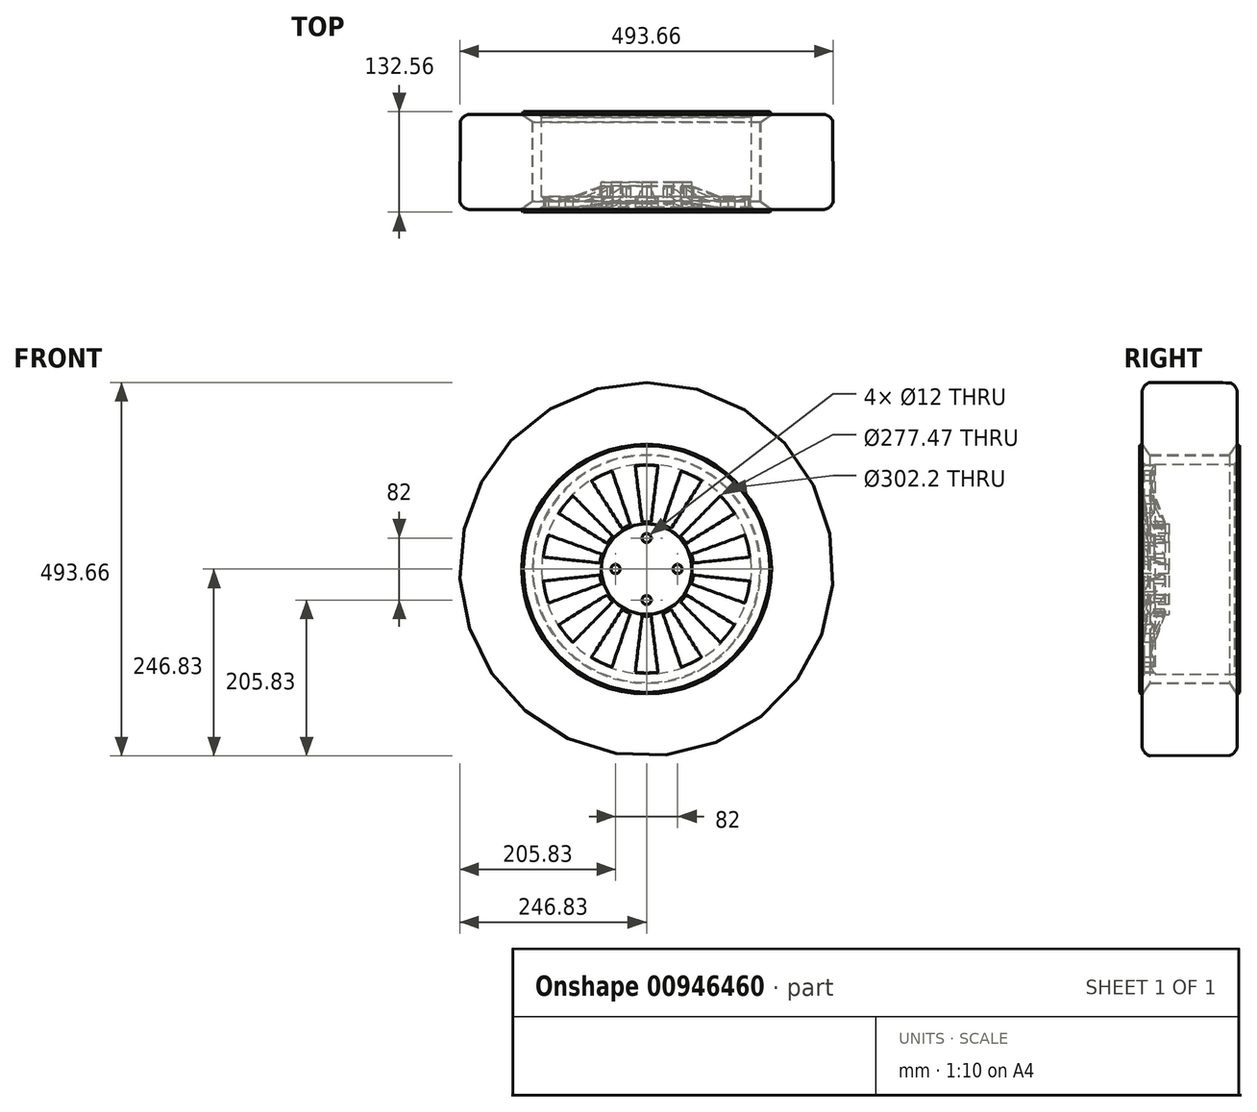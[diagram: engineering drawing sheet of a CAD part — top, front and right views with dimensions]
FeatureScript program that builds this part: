
annotation { "Feature Type Name" : "Feature", "Feature Type Description" : "" }
export const myFeature = defineFeature(function(context is Context, id is Id, definition is map)
    precondition{}
    {
        {
            var Q0;
            Q0=qCreatedBy(makeId("Right.planeOp"),FACE);
            var sketch = newSketch(context, id + "F0", { "sketchPlane" : qUnion([Q0])});
            skLineSegment(sketch, "E0", {"start": v(0, 0) * mm, "end": v(-305.68, 0) * mm, "construction": true});
            skLineSegment(sketch, "E1", {"start": v(-125, 0) * mm, "end": v(-125, 60) * mm});
            skLineSegment(sketch, "E2", {"start": v(-125, 60) * mm, "end": v(-118, 60) * mm});
            skLineSegment(sketch, "E3", {"start": v(0, 0) * mm, "end": v(0, 165.1) * mm, "construction": true});
            skLineSegment(sketch, "E4", {"start": v(0, 165.1) * mm, "end": v(-10.5, 150.1) * mm});
            skLineSegment(sketch, "E5", {"start": v(-10.5, 150.1) * mm, "end": v(-115.5, 150.1) * mm});
            skLineSegment(sketch, "E6", {"start": v(-115.5, 150.1) * mm, "end": v(-126, 165.1) * mm});
            skLineSegment(sketch, "E7", {"start": v(-126, 165.1) * mm, "end": v(-129.28, 162.8) * mm});
            skLineSegment(sketch, "E8", {"start": v(0, 165.1) * mm, "end": v(3.28, 162.8) * mm});
            skLineSegment(sketch, "E9", {"start": v(-129.28, 162.8) * mm, "end": v(-129.28, 147.88) * mm});
            skLineSegment(sketch, "E10", {"start": v(-127.82, 144.34) * mm, "end": v(-123.4, 139.92) * mm});
            skLineSegment(sketch, "E11", {"start": v(-63, 150.1) * mm, "end": v(-63, 101.93) * mm, "construction": true});
            skLineSegment(sketch, "E12.MirrorCS", {"start": v(1.81, 144.34) * mm, "end": v(-3.8, 138.73) * mm});
            skLineSegment(sketch, "E13.MirrorCS", {"start": v(3.28, 162.8) * mm, "end": v(3.28, 147.88) * mm});
            skFitSpline(sketch, "E14", {"points": [v(-118, 60) * mm, v(-127.97, 115.77) * mm, v(-122.21, 138.73) * mm], "startDerivative": vector(-12.1, 140.22) * mm, "endDerivative": vector(53.59, 74.72) * mm});
            skArc(sketch, "E15.filletArc", {"start": v(-123.15, 137.38) * mm, "mid": v(-122.82, 138.7) * mm, "end": v(-123.4, 139.92) * mm});
            skPoint(sketch, "E16.visualSharp", {"position": v(-129.28, 145.8) * mm});
            skArc(sketch, "E16.filletArc", {"start": v(-129.28, 147.88) * mm, "mid": v(-128.9, 145.96) * mm, "end": v(-127.82, 144.34) * mm});
            skPoint(sketch, "E17.visualSharp", {"position": v(3.28, 145.8) * mm});
            skArc(sketch, "E17.filletArc", {"start": v(1.81, 144.34) * mm, "mid": v(2.9, 145.96) * mm, "end": v(3.28, 147.88) * mm});
            skLineSegment(sketch, "E18", {"start": v(-3.8, 138.73) * mm, "end": v(-108.8, 138.73) * mm});
            skLineSegment(sketch, "E19", {"start": v(-95, 60) * mm, "end": v(-90, 60) * mm});
            skLineSegment(sketch, "E20", {"start": v(-90, 60) * mm, "end": v(-90, 0) * mm});
            skLineSegment(sketch, "E21", {"start": v(-90, 0) * mm, "end": v(-125, 0) * mm});
            skFitSpline(sketch, "E22", {"points": [v(-95, 60) * mm, v(-114.6, 118.9) * mm, v(-108.8, 138.73) * mm], "startDerivative": vector(-64.42, 180.65) * mm, "endDerivative": vector(44.77, 42.27) * mm});
            skLineSegment(sketch, "E23", {"start": v(-115.5, 151.1) * mm, "end": v(-10.5, 151.1) * mm});
            skLineSegment(sketch, "E24", {"start": v(-10.5, 151.1) * mm, "end": v(-3.62, 160.93) * mm});
            skLineSegment(sketch, "E25", {"start": v(0, 172.4) * mm, "end": v(0, 232.44) * mm});
            skLineSegment(sketch, "E26", {"start": v(-7.5, 245.43) * mm, "end": v(-7.61, 245.5) * mm});
            skLineSegment(sketch, "E27", {"start": v(-10.08, 246.17) * mm, "end": v(-114.7, 246.83) * mm});
            skLineSegment(sketch, "E28", {"start": v(-118.5, 245.43) * mm, "end": v(-117.24, 246.16) * mm});
            skLineSegment(sketch, "E29", {"start": v(-126, 232.44) * mm, "end": v(-126, 172.4) * mm});
            skLineSegment(sketch, "E30", {"start": v(-122.39, 160.93) * mm, "end": v(-115.5, 151.1) * mm});
            skLineSegment(sketch, "E31", {"start": v(-115.5, 150.1) * mm, "end": v(-115.5, 151.1) * mm});
            skLineSegment(sketch, "E32", {"start": v(-10.5, 150.1) * mm, "end": v(-10.5, 151.1) * mm});
            skPoint(sketch, "E33.visualSharp", {"position": v(-116.06, 246.84) * mm});
            skArc(sketch, "E33.filletArc", {"start": v(-114.7, 246.83) * mm, "mid": v(-116.02, 246.67) * mm, "end": v(-117.24, 246.16) * mm});
            skPoint(sketch, "E34.visualSharp", {"position": v(-8.76, 246.16) * mm});
            skArc(sketch, "E34.filletArc", {"start": v(-7.61, 245.5) * mm, "mid": v(-8.8, 246) * mm, "end": v(-10.08, 246.17) * mm});
            skPoint(sketch, "E35.visualSharp", {"position": v(0, 241.1) * mm});
            skArc(sketch, "E35.filletArc", {"start": v(0, 232.44) * mm, "mid": v(-2, 239.94) * mm, "end": v(-7.5, 245.43) * mm});
            skPoint(sketch, "E36.visualSharp", {"position": v(-126, 241.1) * mm});
            skArc(sketch, "E36.filletArc", {"start": v(-118.5, 245.43) * mm, "mid": v(-124, 239.94) * mm, "end": v(-126, 232.44) * mm});
            skPoint(sketch, "E37.visualSharp", {"position": v(-126, 166.1) * mm});
            skArc(sketch, "E37.filletArc", {"start": v(-126, 172.4) * mm, "mid": v(-125.08, 166.4) * mm, "end": v(-122.39, 160.93) * mm});
            skPoint(sketch, "E38.visualSharp", {"position": v(0, 166.1) * mm});
            skArc(sketch, "E38.filletArc", {"start": v(-3.62, 160.93) * mm, "mid": v(-0.93, 166.4) * mm, "end": v(0, 172.4) * mm});
            skSolve(sketch);
        }
        {
            var Q0;
            Q0=makeQuery(id+"F0.imprint","IMPRINT",FACE,{"disambiguationData":[TD([[makeQuery(id+"F0.imprint","IMPRINT",EDGE,{"derivedFrom":sQuery(id+"F0.wireOp",EDGE,"E23")}),1.0]])]});
            var Q1;
            Q1=makeQuery(id+"F0.imprint","IMPRINT",FACE,{"disambiguationData":[TD([[makeQuery(id+"F0.imprint","IMPRINT",EDGE,{"derivedFrom":sQuery(id+"F0.wireOp",EDGE,"E1")}),-1.0]])]});
            var Q2;
            Q2=sQuery(id+"F0.wireOp",EDGE,"E0");
            revolve(context, id + "F1", {"surfaceOperationType" : NewSurfaceOperationType.NEW, "entities" : qUnion([Q0, Q1]), "axis" : qUnion([Q2]), "revolveType" : RevolveType.FULL});
        }
        {
            var Q0;
            Q0=qCreatedBy(makeId("Front.planeOp"),FACE);
            cPlane(context, id + "F2", {"entities" : qUnion([Q0]), "cplaneType" : CPlaneType.OFFSET, "offset" : 140 * mm, "width" : 150 * mm, "height" : 150 * mm});
        }
        {
            var Q0;
            Q0=qCreatedBy(id+"F2.planeOp",FACE);
            var sketch = newSketch(context, id + "F3", { "sketchPlane" : qUnion([Q0])});
            skCircle(sketch, "E39", {"center": v(0, 0) * mm, "radius": 62.5 * mm, "construction": true});
            skCircle(sketch, "E40", {"center": v(0, 0) * mm, "radius": 137.5 * mm, "construction": true});
            skLineSegment(sketch, "E41", {"start": v(0, 62.5) * mm, "end": v(0, 137.5) * mm, "construction": true});
            skLineSegment(sketch, "E42", {"start": v(-6, 62.21) * mm, "end": v(-15, 136.68) * mm});
            skLineSegment(sketch, "E43", {"start": v(-15, 136.68) * mm, "end": v(0, 137.5) * mm});
            skLineSegment(sketch, "E44", {"start": v(-6, 62.21) * mm, "end": v(0, 62.5) * mm});
            skLineSegment(sketch, "E45.MirrorCS", {"start": v(6, 62.21) * mm, "end": v(15, 136.68) * mm});
            skLineSegment(sketch, "E46.MirrorCS", {"start": v(15, 136.68) * mm, "end": v(0, 137.5) * mm});
            skLineSegment(sketch, "E47.MirrorCS", {"start": v(6, 62.21) * mm, "end": v(0, 62.5) * mm});
            skLineSegment(sketch, "E48.1.0", {"start": v(-21.6, 58.65) * mm, "end": v(-27.12, 56.31) * mm});
            skLineSegment(sketch, "E48.1.1", {"start": v(-21.6, 58.65) * mm, "end": v(-45.79, 129.65) * mm});
            skLineSegment(sketch, "E48.1.2", {"start": v(-32.4, 53.45) * mm, "end": v(-27.12, 56.31) * mm});
            skLineSegment(sketch, "E48.1.3", {"start": v(-32.4, 53.45) * mm, "end": v(-72.82, 116.64) * mm});
            skLineSegment(sketch, "E48.1.4", {"start": v(-45.79, 129.65) * mm, "end": v(-59.66, 123.88) * mm});
            skLineSegment(sketch, "E48.1.5", {"start": v(-72.82, 116.64) * mm, "end": v(-59.66, 123.88) * mm});
            skLineSegment(sketch, "E48.2.0", {"start": v(-44.9, 43.47) * mm, "end": v(-48.86, 38.97) * mm});
            skLineSegment(sketch, "E48.2.1", {"start": v(-44.9, 43.47) * mm, "end": v(-97.5, 96.95) * mm});
            skLineSegment(sketch, "E48.2.2", {"start": v(-52.38, 34.1) * mm, "end": v(-48.86, 38.97) * mm});
            skLineSegment(sketch, "E48.2.3", {"start": v(-52.38, 34.1) * mm, "end": v(-116.21, 73.5) * mm});
            skLineSegment(sketch, "E48.2.4", {"start": v(-97.5, 96.95) * mm, "end": v(-107.5, 85.73) * mm});
            skLineSegment(sketch, "E48.2.5", {"start": v(-116.21, 73.5) * mm, "end": v(-107.5, 85.73) * mm});
            skLineSegment(sketch, "E48.3.0", {"start": v(-59.32, 19.69) * mm, "end": v(-60.93, 13.9) * mm});
            skLineSegment(sketch, "E48.3.1", {"start": v(-59.32, 19.69) * mm, "end": v(-129.91, 45.04) * mm});
            skLineSegment(sketch, "E48.3.2", {"start": v(-61.99, 8) * mm, "end": v(-60.93, 13.9) * mm});
            skLineSegment(sketch, "E48.3.3", {"start": v(-61.99, 8) * mm, "end": v(-136.6, 15.8) * mm});
            skLineSegment(sketch, "E48.3.4", {"start": v(-129.91, 45.04) * mm, "end": v(-134.05, 30.6) * mm});
            skLineSegment(sketch, "E48.3.5", {"start": v(-136.6, 15.8) * mm, "end": v(-134.05, 30.6) * mm});
            skLineSegment(sketch, "E48.4.0", {"start": v(-61.99, -8) * mm, "end": v(-60.93, -13.9) * mm});
            skLineSegment(sketch, "E48.4.1", {"start": v(-61.99, -8) * mm, "end": v(-136.6, -15.8) * mm});
            skLineSegment(sketch, "E48.4.2", {"start": v(-59.32, -19.69) * mm, "end": v(-60.93, -13.9) * mm});
            skLineSegment(sketch, "E48.4.3", {"start": v(-59.32, -19.69) * mm, "end": v(-129.91, -45.04) * mm});
            skLineSegment(sketch, "E48.4.4", {"start": v(-136.6, -15.8) * mm, "end": v(-134.05, -30.6) * mm});
            skLineSegment(sketch, "E48.4.5", {"start": v(-129.91, -45.04) * mm, "end": v(-134.05, -30.6) * mm});
            skLineSegment(sketch, "E48.5.0", {"start": v(-52.38, -34.1) * mm, "end": v(-48.86, -38.97) * mm});
            skLineSegment(sketch, "E48.5.1", {"start": v(-52.38, -34.1) * mm, "end": v(-116.21, -73.5) * mm});
            skLineSegment(sketch, "E48.5.2", {"start": v(-44.9, -43.47) * mm, "end": v(-48.86, -38.97) * mm});
            skLineSegment(sketch, "E48.5.3", {"start": v(-44.9, -43.47) * mm, "end": v(-97.5, -96.95) * mm});
            skLineSegment(sketch, "E48.5.4", {"start": v(-116.21, -73.5) * mm, "end": v(-107.5, -85.73) * mm});
            skLineSegment(sketch, "E48.5.5", {"start": v(-97.5, -96.95) * mm, "end": v(-107.5, -85.73) * mm});
            skLineSegment(sketch, "E48.6.0", {"start": v(-32.4, -53.45) * mm, "end": v(-27.12, -56.31) * mm});
            skLineSegment(sketch, "E48.6.1", {"start": v(-32.4, -53.45) * mm, "end": v(-72.82, -116.64) * mm});
            skLineSegment(sketch, "E48.6.2", {"start": v(-21.6, -58.65) * mm, "end": v(-27.12, -56.31) * mm});
            skLineSegment(sketch, "E48.6.3", {"start": v(-21.6, -58.65) * mm, "end": v(-45.79, -129.65) * mm});
            skLineSegment(sketch, "E48.6.4", {"start": v(-72.82, -116.64) * mm, "end": v(-59.66, -123.88) * mm});
            skLineSegment(sketch, "E48.6.5", {"start": v(-45.79, -129.65) * mm, "end": v(-59.66, -123.88) * mm});
            skLineSegment(sketch, "E48.7.0", {"start": v(-6, -62.21) * mm, "end": v(0, -62.5) * mm});
            skLineSegment(sketch, "E48.7.1", {"start": v(-6, -62.21) * mm, "end": v(-15, -136.68) * mm});
            skLineSegment(sketch, "E48.7.2", {"start": v(6, -62.21) * mm, "end": v(0, -62.5) * mm});
            skLineSegment(sketch, "E48.7.3", {"start": v(6, -62.21) * mm, "end": v(15, -136.68) * mm});
            skLineSegment(sketch, "E48.7.4", {"start": v(-15, -136.68) * mm, "end": v(0, -137.5) * mm});
            skLineSegment(sketch, "E48.7.5", {"start": v(15, -136.68) * mm, "end": v(0, -137.5) * mm});
            skLineSegment(sketch, "E48.8.0", {"start": v(21.6, -58.65) * mm, "end": v(27.12, -56.31) * mm});
            skLineSegment(sketch, "E48.8.1", {"start": v(21.6, -58.65) * mm, "end": v(45.79, -129.65) * mm});
            skLineSegment(sketch, "E48.8.2", {"start": v(32.4, -53.45) * mm, "end": v(27.12, -56.31) * mm});
            skLineSegment(sketch, "E48.8.3", {"start": v(32.4, -53.45) * mm, "end": v(72.82, -116.64) * mm});
            skLineSegment(sketch, "E48.8.4", {"start": v(45.79, -129.65) * mm, "end": v(59.66, -123.88) * mm});
            skLineSegment(sketch, "E48.8.5", {"start": v(72.82, -116.64) * mm, "end": v(59.66, -123.88) * mm});
            skLineSegment(sketch, "E48.9.0", {"start": v(44.9, -43.47) * mm, "end": v(48.86, -38.97) * mm});
            skLineSegment(sketch, "E48.9.1", {"start": v(44.9, -43.47) * mm, "end": v(97.5, -96.95) * mm});
            skLineSegment(sketch, "E48.9.2", {"start": v(52.38, -34.1) * mm, "end": v(48.86, -38.97) * mm});
            skLineSegment(sketch, "E48.9.3", {"start": v(52.38, -34.1) * mm, "end": v(116.21, -73.5) * mm});
            skLineSegment(sketch, "E48.9.4", {"start": v(97.5, -96.95) * mm, "end": v(107.5, -85.73) * mm});
            skLineSegment(sketch, "E48.9.5", {"start": v(116.21, -73.5) * mm, "end": v(107.5, -85.73) * mm});
            skLineSegment(sketch, "E48.10.0", {"start": v(59.32, -19.69) * mm, "end": v(60.93, -13.9) * mm});
            skLineSegment(sketch, "E48.10.1", {"start": v(59.32, -19.69) * mm, "end": v(129.91, -45.04) * mm});
            skLineSegment(sketch, "E48.10.2", {"start": v(61.99, -8) * mm, "end": v(60.93, -13.9) * mm});
            skLineSegment(sketch, "E48.10.3", {"start": v(61.99, -8) * mm, "end": v(136.6, -15.8) * mm});
            skLineSegment(sketch, "E48.10.4", {"start": v(129.91, -45.04) * mm, "end": v(134.05, -30.6) * mm});
            skLineSegment(sketch, "E48.10.5", {"start": v(136.6, -15.8) * mm, "end": v(134.05, -30.6) * mm});
            skLineSegment(sketch, "E48.11.0", {"start": v(61.99, 8) * mm, "end": v(60.93, 13.9) * mm});
            skLineSegment(sketch, "E48.11.1", {"start": v(61.99, 8) * mm, "end": v(136.6, 15.8) * mm});
            skLineSegment(sketch, "E48.11.2", {"start": v(59.32, 19.69) * mm, "end": v(60.93, 13.9) * mm});
            skLineSegment(sketch, "E48.11.3", {"start": v(59.32, 19.69) * mm, "end": v(129.91, 45.04) * mm});
            skLineSegment(sketch, "E48.11.4", {"start": v(136.6, 15.8) * mm, "end": v(134.05, 30.6) * mm});
            skLineSegment(sketch, "E48.11.5", {"start": v(129.91, 45.04) * mm, "end": v(134.05, 30.6) * mm});
            skLineSegment(sketch, "E48.12.0", {"start": v(52.38, 34.1) * mm, "end": v(48.86, 38.97) * mm});
            skLineSegment(sketch, "E48.12.1", {"start": v(52.38, 34.1) * mm, "end": v(116.21, 73.5) * mm});
            skLineSegment(sketch, "E48.12.2", {"start": v(44.9, 43.47) * mm, "end": v(48.86, 38.97) * mm});
            skLineSegment(sketch, "E48.12.3", {"start": v(44.9, 43.47) * mm, "end": v(97.5, 96.95) * mm});
            skLineSegment(sketch, "E48.12.4", {"start": v(116.21, 73.5) * mm, "end": v(107.5, 85.73) * mm});
            skLineSegment(sketch, "E48.12.5", {"start": v(97.5, 96.95) * mm, "end": v(107.5, 85.73) * mm});
            skLineSegment(sketch, "E48.13.0", {"start": v(32.4, 53.45) * mm, "end": v(27.12, 56.31) * mm});
            skLineSegment(sketch, "E48.13.1", {"start": v(32.4, 53.45) * mm, "end": v(72.82, 116.64) * mm});
            skLineSegment(sketch, "E48.13.2", {"start": v(21.6, 58.65) * mm, "end": v(27.12, 56.31) * mm});
            skLineSegment(sketch, "E48.13.3", {"start": v(21.6, 58.65) * mm, "end": v(45.79, 129.65) * mm});
            skLineSegment(sketch, "E48.13.4", {"start": v(72.82, 116.64) * mm, "end": v(59.66, 123.88) * mm});
            skLineSegment(sketch, "E48.13.5", {"start": v(45.79, 129.65) * mm, "end": v(59.66, 123.88) * mm});
            skSolve(sketch);
        }
        {
            var Q0;
            Q0=makeQuery(id+"F3.imprint","IMPRINT",FACE,{"disambiguationData":[TD([[makeQuery(id+"F3.imprint","IMPRINT",EDGE,{"derivedFrom":sQuery(id+"F3.wireOp",EDGE,"E48.1.0")}),-1.0]])]});
            var Q1;
            Q1=makeQuery(id+"F3.imprint","IMPRINT",FACE,{"disambiguationData":[TD([[makeQuery(id+"F3.imprint","IMPRINT",EDGE,{"derivedFrom":sQuery(id+"F3.wireOp",EDGE,"E42")}),-1.0]])]});
            var Q2;
            Q2=makeQuery(id+"F3.imprint","IMPRINT",FACE,{"disambiguationData":[TD([[makeQuery(id+"F3.imprint","IMPRINT",EDGE,{"derivedFrom":sQuery(id+"F3.wireOp",EDGE,"E48.13.0")}),-1.0]])]});
            var Q3;
            Q3=makeQuery(id+"F3.imprint","IMPRINT",FACE,{"disambiguationData":[TD([[makeQuery(id+"F3.imprint","IMPRINT",EDGE,{"derivedFrom":sQuery(id+"F3.wireOp",EDGE,"E48.12.0")}),-1.0]])]});
            var Q4;
            Q4=makeQuery(id+"F3.imprint","IMPRINT",FACE,{"disambiguationData":[TD([[makeQuery(id+"F3.imprint","IMPRINT",EDGE,{"derivedFrom":sQuery(id+"F3.wireOp",EDGE,"E48.11.0")}),-1.0]])]});
            var Q5;
            Q5=makeQuery(id+"F3.imprint","IMPRINT",FACE,{"disambiguationData":[TD([[makeQuery(id+"F3.imprint","IMPRINT",EDGE,{"derivedFrom":sQuery(id+"F3.wireOp",EDGE,"E48.10.0")}),-1.0]])]});
            var Q6;
            Q6=makeQuery(id+"F3.imprint","IMPRINT",FACE,{"disambiguationData":[TD([[makeQuery(id+"F3.imprint","IMPRINT",EDGE,{"derivedFrom":sQuery(id+"F3.wireOp",EDGE,"E48.9.0")}),-1.0]])]});
            var Q7;
            Q7=makeQuery(id+"F3.imprint","IMPRINT",FACE,{"disambiguationData":[TD([[makeQuery(id+"F3.imprint","IMPRINT",EDGE,{"derivedFrom":sQuery(id+"F3.wireOp",EDGE,"E48.8.0")}),-1.0]])]});
            var Q8;
            Q8=makeQuery(id+"F3.imprint","IMPRINT",FACE,{"disambiguationData":[TD([[makeQuery(id+"F3.imprint","IMPRINT",EDGE,{"derivedFrom":sQuery(id+"F3.wireOp",EDGE,"E48.7.0")}),-1.0]])]});
            var Q9;
            Q9=makeQuery(id+"F3.imprint","IMPRINT",FACE,{"disambiguationData":[TD([[makeQuery(id+"F3.imprint","IMPRINT",EDGE,{"derivedFrom":sQuery(id+"F3.wireOp",EDGE,"E48.6.0")}),-1.0]])]});
            var Q10;
            Q10=makeQuery(id+"F3.imprint","IMPRINT",FACE,{"disambiguationData":[TD([[makeQuery(id+"F3.imprint","IMPRINT",EDGE,{"derivedFrom":sQuery(id+"F3.wireOp",EDGE,"E48.5.0")}),-1.0]])]});
            var Q11;
            Q11=makeQuery(id+"F3.imprint","IMPRINT",FACE,{"disambiguationData":[TD([[makeQuery(id+"F3.imprint","IMPRINT",EDGE,{"derivedFrom":sQuery(id+"F3.wireOp",EDGE,"E48.4.0")}),-1.0]])]});
            var Q12;
            Q12=makeQuery(id+"F3.imprint","IMPRINT",FACE,{"disambiguationData":[TD([[makeQuery(id+"F3.imprint","IMPRINT",EDGE,{"derivedFrom":sQuery(id+"F3.wireOp",EDGE,"E48.3.0")}),-1.0]])]});
            var Q13;
            Q13=makeQuery(id+"F3.imprint","IMPRINT",FACE,{"disambiguationData":[TD([[makeQuery(id+"F3.imprint","IMPRINT",EDGE,{"derivedFrom":sQuery(id+"F3.wireOp",EDGE,"E48.2.0")}),-1.0]])]});
            extrude(context, id + "F4", {"entities" : qUnion([Q0, Q1, Q2, Q3, Q4, Q5, Q6, Q7, Q8, Q9, Q10, Q11, Q12, Q13]), "operationType" : NewBodyOperationType.REMOVE, "oppositeDirection" : true, "depth" : 150 * mm, "offsetDistance" : 25 * mm});
        }
        {
            var Q0;
            Q0=makeQuery(id+"F1.opRevolve","SWEPT_FACE",FACE,{"disambiguationData":[OSD([sQuery(id+"F0.wireOp",EDGE,"E1")])]});
            var sketch = newSketch(context, id + "F5", { "sketchPlane" : qUnion([Q0])});
            skLineSegment(sketch, "E49", {"start": v(0, 0) * mm, "end": v(0, 41) * mm, "construction": true});
            skCircle(sketch, "E50", {"center": v(0, 41) * mm, "radius": 6 * mm});
            skCircle(sketch, "E51.1.0", {"center": v(-41, 0) * mm, "radius": 6 * mm});
            skCircle(sketch, "E51.2.0", {"center": v(0, -41) * mm, "radius": 6 * mm});
            skCircle(sketch, "E51.3.0", {"center": v(41, 0) * mm, "radius": 6 * mm});
            skPoint(sketch, "E51.center", {"position": v(0, 0) * mm});
            skSolve(sketch);
        }
        {
            var Q0;
            Q0=makeQuery(id+"F5.imprint","IMPRINT",FACE,{"disambiguationData":[TD([[makeQuery(id+"F5.imprint","IMPRINT",EDGE,{"derivedFrom":sQuery(id+"F5.wireOp",EDGE,"E50")}),1.0]])]});
            var Q1;
            Q1=makeQuery(id+"F5.imprint","IMPRINT",FACE,{"disambiguationData":[TD([[makeQuery(id+"F5.imprint","IMPRINT",EDGE,{"derivedFrom":sQuery(id+"F5.wireOp",EDGE,"E51.3.0")}),1.0]])]});
            var Q2;
            Q2=makeQuery(id+"F5.imprint","IMPRINT",FACE,{"disambiguationData":[TD([[makeQuery(id+"F5.imprint","IMPRINT",EDGE,{"derivedFrom":sQuery(id+"F5.wireOp",EDGE,"E51.2.0")}),1.0]])]});
            var Q3;
            Q3=makeQuery(id+"F5.imprint","IMPRINT",FACE,{"disambiguationData":[TD([[makeQuery(id+"F5.imprint","IMPRINT",EDGE,{"derivedFrom":sQuery(id+"F5.wireOp",EDGE,"E51.1.0")}),1.0]])]});
            extrude(context, id + "F6", {"entities" : qUnion([Q0, Q1, Q2, Q3]), "operationType" : NewBodyOperationType.REMOVE, "oppositeDirection" : true, "depth" : 150 * mm, "offsetDistance" : 25 * mm});
        }
        {
            var Q0;
            Q0=makeQuery(id+"F1.opRevolve","SWEPT_EDGE",EDGE,{"disambiguationData":[OSD([sQuery(id+"F0.wireOp",EDGE,"E1"),sQuery(id+"F0.wireOp",EDGE,"E2")])]});
            fillet(context, id + "F7", {"entities" : qUnion([Q0]), "radius" : 2 * mm, "tangentPropagation" : true, "rho" : 0.1, "crossSection" : FilletCrossSection.CONIC, "allowEdgeOverflow" : false});
        }
    });
